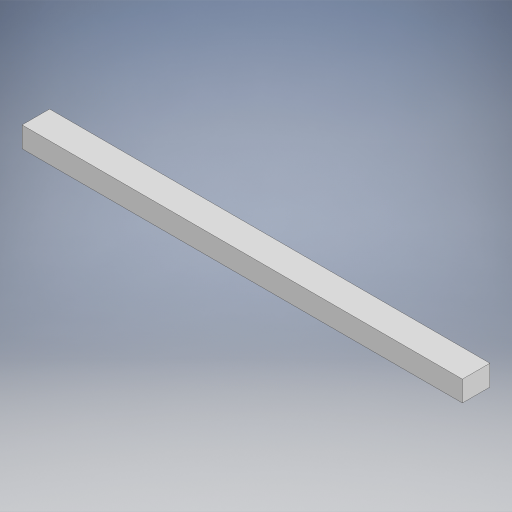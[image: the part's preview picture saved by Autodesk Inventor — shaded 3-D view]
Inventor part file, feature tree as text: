
AUTODESK INVENTOR PART (.ipt)
format: ipt  version: 2023.1 (Build 271208000, 208)  size: 247,296 bytes
history: native  units: in
note: dims shown in document units (in); Inventor stores cm internally (conversion verified against a paired STEP export)
features: extrude x1, sketch x1
ambient origin geometry x8: Origin, YZ Plane, XZ Plane, XY Plane, X Axis, Y Axis, Z Axis, Center Point
bodies: Solid1 (feature_tree)
feature tree (2):
  extrude  "Extrusion1"  Depth=3.0in
  sketch  "Sketch1"  dims[d0=2.25in d1=3.0in d2=48.0in d3=0.0in]
